# Revit family: Haworth_Masters_Tackboard
name_source: partatom
category: Furniture Systems
revit_build: Autodesk Revit 2018 (Build: 20170223_1515(x64)
units: mm (PartAtom-declared; Revit-internal decimal feet)

## family parameters
Always vertical = Yes
Cut with Voids When Loaded = No
OmniClass Number = 23.40.70.14.64.21
OmniClass Title = Systems Furniture
Part Type = Normal
Room Calculation Point = No
Round Connector Dimension = Use Diameter
Shared = No
Work Plane-Based = No

## types (2) — shared parameters
Actual Height = 24"
Actual Width = 27 1/2"
Assembly Code = E2020200
Description = Haworth - Masters - Tackboard
Manufacturer = Haworth
Max. Width = 96"
Min. Width = 27 1/2"
Model = Haworth - Masters - Tackboard
Revision Number = 3
Size = Verify Final Dim. w/ Haworth
Slat Rail = Haworth - Slat Tile
Slats = No
Standard Height OSU = OSU: 22 in
Standard Height VSU = VSU: 24 in
Standard Widths OSU = OSU: 30-120 in @ 6 in increments
Standard Widths VSU = VSU: 27 1/2-93 1/2 in @ 6 in increments
Sustainability Info = http://www.haworth.com
Tackboard Finish = Haworth _ Fabric _ Tellure _ Sky 3A-32
Tackboard Height = 24"
URL = www.haworth.com
URL - Product = http://www.haworth.com
Warranty = http://www.haworth.com
Width = 27 1/2"

## type names (no varying parameters)
- 24" Tackboard
- 24" Tackboard w/ Slat Rail

## geometry (parser evidence)
native form markers: Sweep x3
no freeform markers — native parametric forms only
